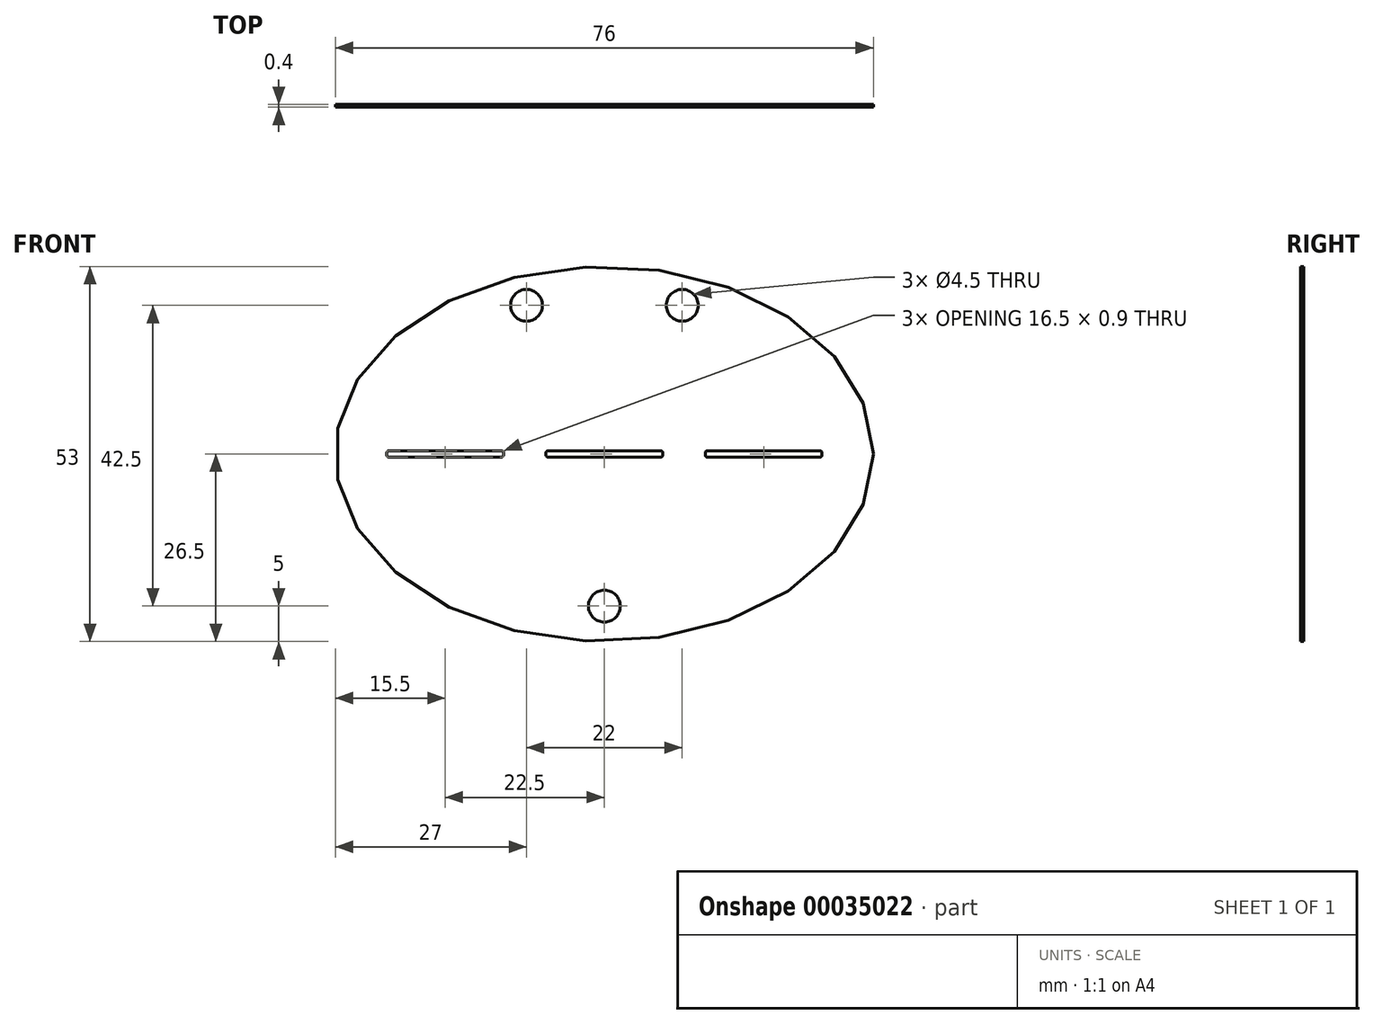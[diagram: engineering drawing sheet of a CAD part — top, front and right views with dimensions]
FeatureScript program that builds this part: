
annotation { "Feature Type Name" : "Feature", "Feature Type Description" : "" }
export const myFeature = defineFeature(function(context is Context, id is Id, definition is map)
    precondition{}
    {
        {
            var Q0;
            Q0=qCreatedBy(makeId("Front.planeOp"),FACE);
            var sketch = newSketch(context, id + "F0", { "sketchPlane" : qUnion([Q0])});
            skEllipse(sketch, "E0", {"center": v(0, 0) * mm, "majorRadius": 38 * mm, "minorRadius": 26.5 * mm, "majorAxis": v(1, 0)});
            skLineSegment(sketch, "E1.rect.bottom", {"start": v(7.95, -0.45) * mm, "end": v(-7.95, -0.45) * mm});
            skLineSegment(sketch, "E1.rect.top", {"start": v(7.95, 0.45) * mm, "end": v(-7.95, 0.45) * mm});
            skLineSegment(sketch, "E1.rect.left", {"start": v(8.25, -0.15) * mm, "end": v(8.25, 0.15) * mm});
            skLineSegment(sketch, "E1.rect.right", {"start": v(-8.25, -0.15) * mm, "end": v(-8.25, 0.15) * mm});
            skLineSegment(sketch, "E2.rect.bottom", {"start": v(30.45, -0.45) * mm, "end": v(14.55, -0.45) * mm});
            skLineSegment(sketch, "E2.rect.top", {"start": v(30.45, 0.45) * mm, "end": v(14.55, 0.45) * mm});
            skLineSegment(sketch, "E2.rect.left", {"start": v(30.75, -0.15) * mm, "end": v(30.75, 0.15) * mm});
            skLineSegment(sketch, "E2.rect.right", {"start": v(14.25, -0.15) * mm, "end": v(14.25, 0.15) * mm});
            skPoint(sketch, "E2.rect.middle", {"position": v(22.5, 0) * mm});
            skLineSegment(sketch, "E3.MirrorCS", {"start": v(-30.45, 0.45) * mm, "end": v(-14.55, 0.45) * mm});
            skLineSegment(sketch, "E4.MirrorCS", {"start": v(-30.45, -0.45) * mm, "end": v(-14.55, -0.45) * mm});
            skLineSegment(sketch, "E5.MirrorCS", {"start": v(-14.25, -0.15) * mm, "end": v(-14.25, 0.15) * mm});
            skLineSegment(sketch, "E6.MirrorCS", {"start": v(-30.75, -0.15) * mm, "end": v(-30.75, 0.15) * mm});
            skCircle(sketch, "E7", {"center": v(0, -21.5) * mm, "radius": 2.25 * mm});
            skCircle(sketch, "E8", {"center": v(-11, 21) * mm, "radius": 2.25 * mm});
            skCircle(sketch, "E9.MirrorC", {"center": v(11, 21) * mm, "radius": 2.25 * mm});
            skPoint(sketch, "E10.visualSharp", {"position": v(-30.75, 0.45) * mm});
            skArc(sketch, "E10.filletArc", {"start": v(-30.45, 0.45) * mm, "mid": v(-30.66, 0.36) * mm, "end": v(-30.75, 0.15) * mm});
            skPoint(sketch, "E11.visualSharp", {"position": v(-30.75, -0.45) * mm});
            skArc(sketch, "E11.filletArc", {"start": v(-30.75, -0.15) * mm, "mid": v(-30.66, -0.36) * mm, "end": v(-30.45, -0.45) * mm});
            skPoint(sketch, "E12.visualSharp", {"position": v(-14.25, 0.45) * mm});
            skArc(sketch, "E12.filletArc", {"start": v(-14.25, 0.15) * mm, "mid": v(-14.34, 0.36) * mm, "end": v(-14.55, 0.45) * mm});
            skPoint(sketch, "E13.visualSharp", {"position": v(-14.25, -0.45) * mm});
            skArc(sketch, "E13.filletArc", {"start": v(-14.55, -0.45) * mm, "mid": v(-14.34, -0.36) * mm, "end": v(-14.25, -0.15) * mm});
            skPoint(sketch, "E14.visualSharp", {"position": v(14.25, -0.45) * mm});
            skArc(sketch, "E14.filletArc", {"start": v(14.25, -0.15) * mm, "mid": v(14.34, -0.36) * mm, "end": v(14.55, -0.45) * mm});
            skPoint(sketch, "E15.visualSharp", {"position": v(14.25, 0.45) * mm});
            skArc(sketch, "E15.filletArc", {"start": v(14.55, 0.45) * mm, "mid": v(14.34, 0.36) * mm, "end": v(14.25, 0.15) * mm});
            skPoint(sketch, "E16.visualSharp", {"position": v(30.75, 0.45) * mm});
            skArc(sketch, "E16.filletArc", {"start": v(30.75, 0.15) * mm, "mid": v(30.66, 0.36) * mm, "end": v(30.45, 0.45) * mm});
            skPoint(sketch, "E17.visualSharp", {"position": v(30.75, -0.45) * mm});
            skArc(sketch, "E17.filletArc", {"start": v(30.45, -0.45) * mm, "mid": v(30.66, -0.36) * mm, "end": v(30.75, -0.15) * mm});
            skPoint(sketch, "E18.visualSharp", {"position": v(-8.25, 0.45) * mm});
            skArc(sketch, "E18.filletArc", {"start": v(-7.95, 0.45) * mm, "mid": v(-8.16, 0.36) * mm, "end": v(-8.25, 0.15) * mm});
            skPoint(sketch, "E19.visualSharp", {"position": v(-8.25, -0.45) * mm});
            skArc(sketch, "E19.filletArc", {"start": v(-8.25, -0.15) * mm, "mid": v(-8.16, -0.36) * mm, "end": v(-7.95, -0.45) * mm});
            skPoint(sketch, "E20.visualSharp", {"position": v(8.25, 0.45) * mm});
            skArc(sketch, "E20.filletArc", {"start": v(8.25, 0.15) * mm, "mid": v(8.16, 0.36) * mm, "end": v(7.95, 0.45) * mm});
            skPoint(sketch, "E21.visualSharp", {"position": v(8.25, -0.45) * mm});
            skArc(sketch, "E21.filletArc", {"start": v(7.95, -0.45) * mm, "mid": v(8.16, -0.36) * mm, "end": v(8.25, -0.15) * mm});
            skSolve(sketch);
        }
        {
            var Q0;
            Q0=makeQuery(id+"F0.imprint","IMPRINT",FACE,{"disambiguationData":[TD([[makeQuery(id+"F0.imprint","IMPRINT",EDGE,{"derivedFrom":sQuery(id+"F0.wireOp",EDGE,"E0")}),1.0]])]});
            extrude(context, id + "F1", {"entities" : qUnion([Q0]), "depth" : 0.4 * mm});
        }
    });
